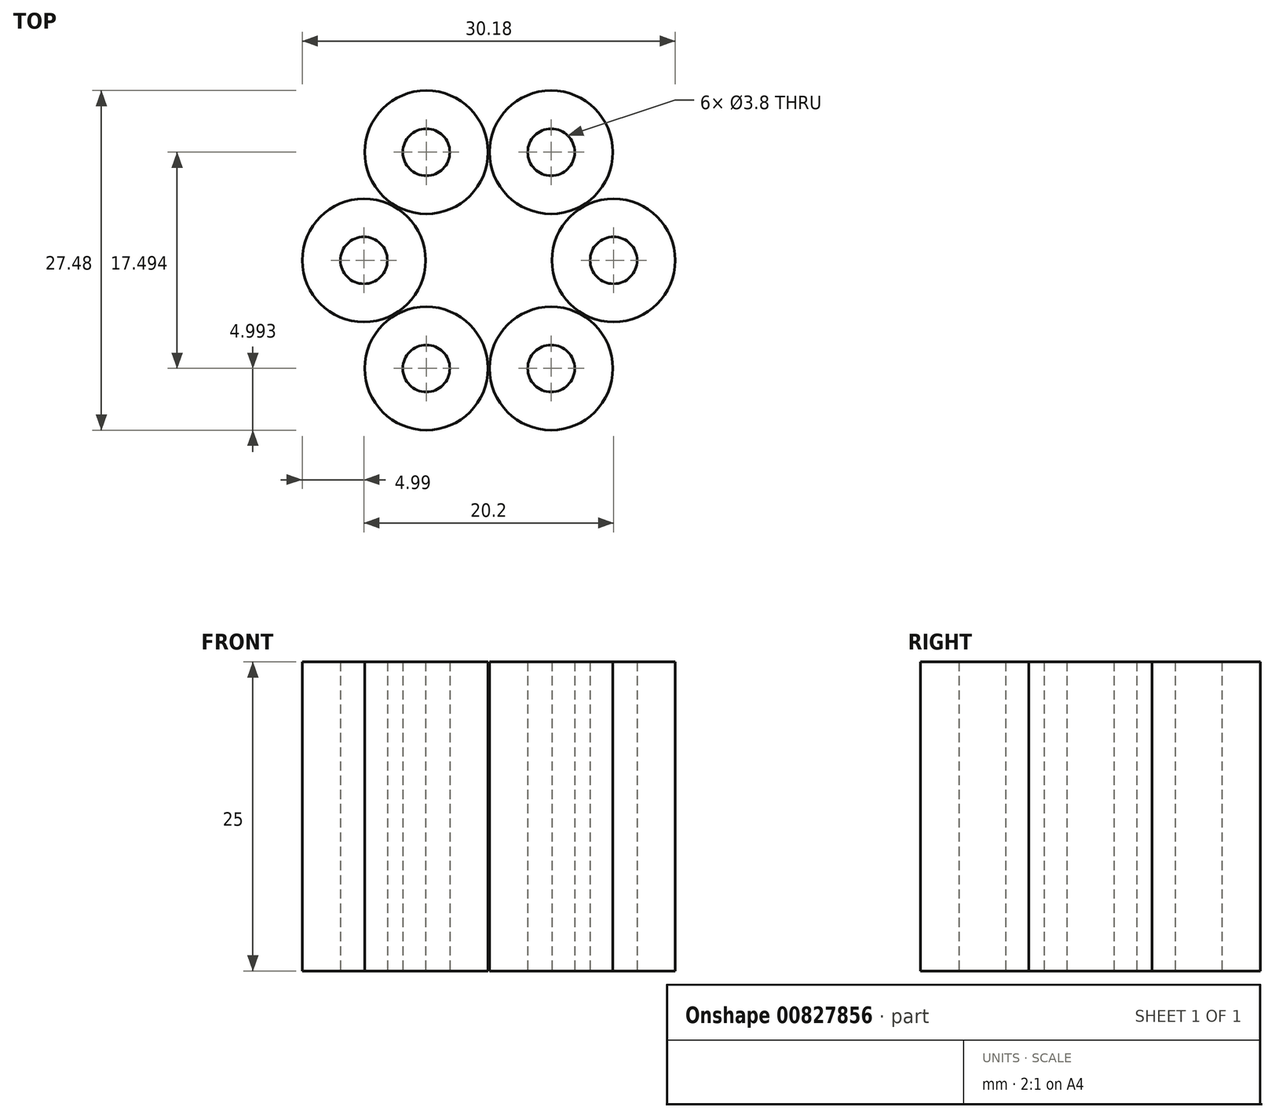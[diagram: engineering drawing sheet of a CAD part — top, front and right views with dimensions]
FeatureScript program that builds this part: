
annotation { "Feature Type Name" : "Feature", "Feature Type Description" : "" }
export const myFeature = defineFeature(function(context is Context, id is Id, definition is map)
    precondition{}
    {
        {
            var Q0;
            Q0=qCreatedBy(makeId("Top.planeOp"),FACE);
            var sketch = newSketch(context, id + "F0", { "sketchPlane" : qUnion([Q0])});
            skCircle(sketch, "E0", {"center": v(10.1, 0) * mm, "radius": 5 * mm});
            skCircle(sketch, "E1", {"center": v(10.1, 0) * mm, "radius": 1.9 * mm});
            skCircle(sketch, "E2.1.0", {"center": v(5.05, 8.75) * mm, "radius": 5 * mm});
            skCircle(sketch, "E2.1.1", {"center": v(5.05, 8.75) * mm, "radius": 1.9 * mm});
            skCircle(sketch, "E2.2.0", {"center": v(-5.05, 8.75) * mm, "radius": 5 * mm});
            skCircle(sketch, "E2.2.1", {"center": v(-5.05, 8.75) * mm, "radius": 1.9 * mm});
            skPoint(sketch, "E2.center", {"position": v(0, 0) * mm});
            skCircle(sketch, "E3.1.3.0", {"center": v(-10.1, 0) * mm, "radius": 5 * mm});
            skCircle(sketch, "E3.2.3.0", {"center": v(-10.1, 0) * mm, "radius": 1.9 * mm});
            skCircle(sketch, "E3.1.4.0", {"center": v(-5.05, -8.75) * mm, "radius": 5 * mm});
            skCircle(sketch, "E3.2.4.0", {"center": v(-5.05, -8.75) * mm, "radius": 1.9 * mm});
            skCircle(sketch, "E3.1.5.0", {"center": v(5.05, -8.75) * mm, "radius": 5 * mm});
            skCircle(sketch, "E3.2.5.0", {"center": v(5.05, -8.75) * mm, "radius": 1.9 * mm});
            skSolve(sketch);
        }
        {
            var Q0;
            Q0 = qSketchRegion(id + "F0", true);
            extrude(context, id + "F1", {"entities" : qUnion([Q0]), "depth" : 25 * mm, "offsetDistance" : 25 * mm});
        }
    });
